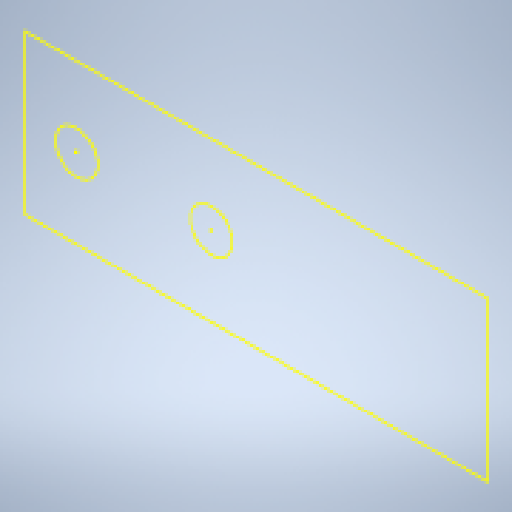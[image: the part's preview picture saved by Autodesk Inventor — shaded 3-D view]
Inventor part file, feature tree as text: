
AUTODESK INVENTOR PART (.ipt)
format: ipt  version: 2024.3 (Build 283343000, 343)  size: 125,952 bytes
history: native  units: mm
features: other x2, sketch x1, reference x1
ambient origin geometry x8: Origin, YZ Plane, XZ Plane, XY Plane, X Axis, Y Axis, Z Axis, Center Point
feature tree (4):
  sketch  "Sketch1"
  reference  "Reference1"
  other  "Assembly1"
  other  "dedos_MIR:1"
